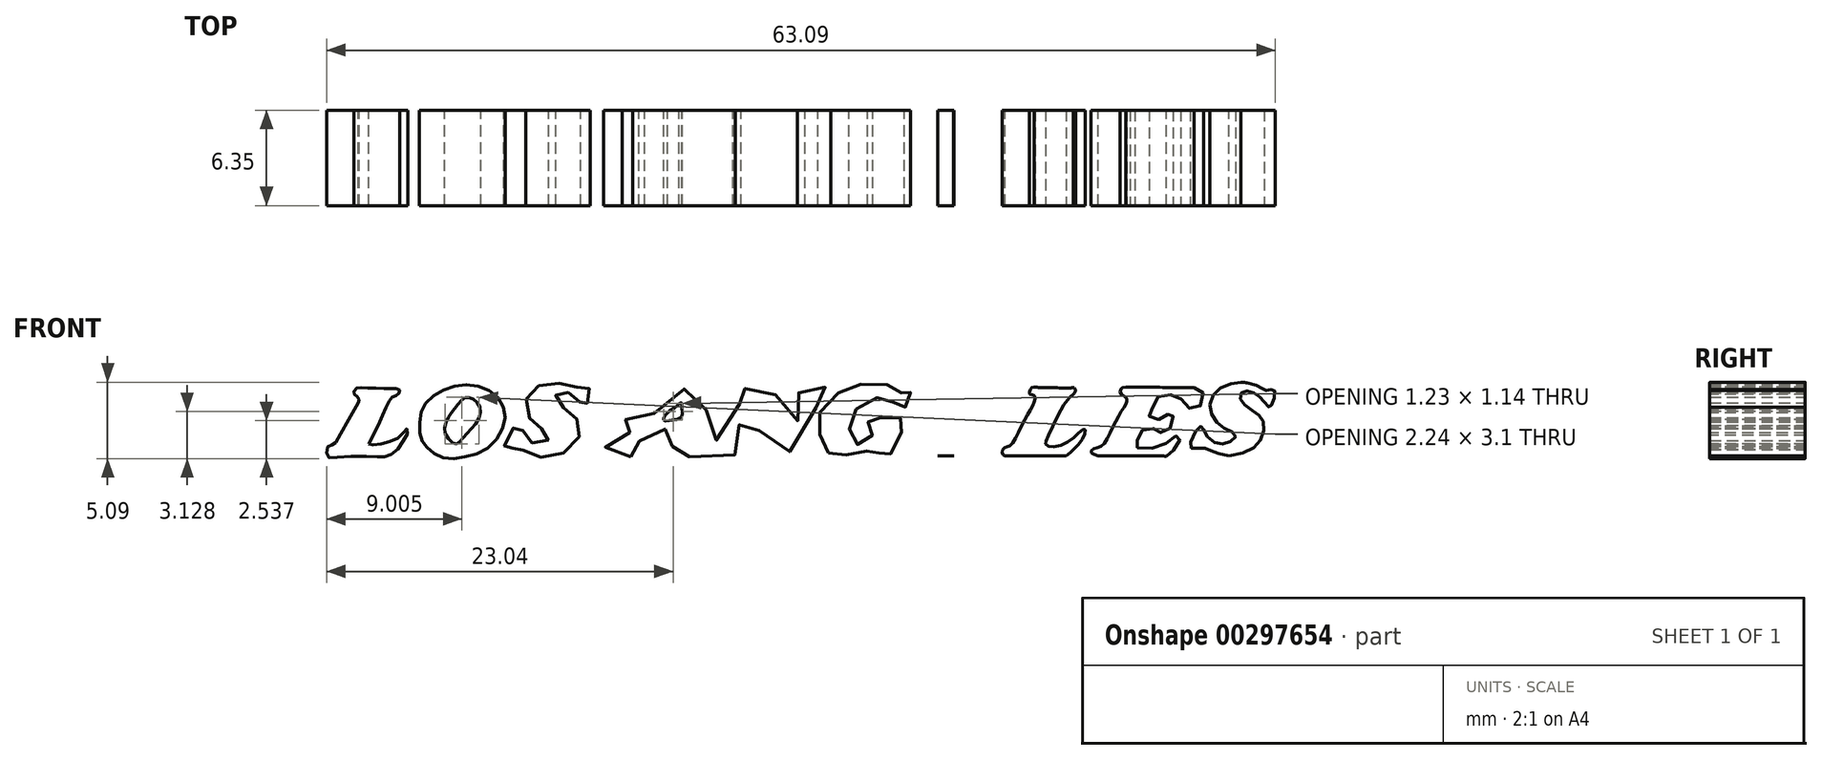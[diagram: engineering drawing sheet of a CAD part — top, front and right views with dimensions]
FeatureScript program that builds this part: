
annotation { "Feature Type Name" : "Feature", "Feature Type Description" : "" }
export const myFeature = defineFeature(function(context is Context, id is Id, definition is map)
    precondition{}
    {
        {
            var Q0;
            Q0=qCreatedBy(makeId("Front.planeOp"),FACE);
            var sketch = newSketch(context, id + "F0", { "sketchPlane" : qUnion([Q0])});
            skFitSpline(sketch, "E0", {"points": [v(-42.48, -14.81) * mm, v(-28.24, -14.72) * mm, v(-25.29, -14.85) * mm, v(-23.97, -14.75) * mm, v(-23, -13.63) * mm, v(-21.37, -10.74) * mm, v(-20.73, -9.87) * mm, v(-20.5, -9.65) * mm, v(-19.83, -9.62) * mm, v(-15.31, -9.65) * mm, v(-11.17, -9.59) * mm, v(-7.2, -9.59) * mm, v(-6.43, -9.55) * mm, v(-6.07, -9.4) * mm, v(-5.94, -9) * mm, v(-6.65, -8.5) * mm, v(-7.13, -8.34) * mm, v(-7.32, -7.4) * mm, v(-7.07, -6.73) * mm, v(-6.33, -5.29) * mm, v(-5.34, -3.5) * mm, v(-4.63, -2.34) * mm, v(-4.44, -1.86) * mm, v(-4.18, -1.82) * mm, v(-4.05, -2.63) * mm, v(-3.54, -5.03) * mm, v(-3.12, -7.28) * mm, v(-2.77, -8.75) * mm, v(-2.16, -9.36) * mm, v(-1.2, -9.65) * mm, v(0, -9.59) * mm, v(1.88, -9.62) * mm, v(5.82, -9.54) * mm, v(10.32, -9.56) * mm, v(13.02, -9.67) * mm, v(13.61, -9.46) * mm, v(13.97, -9.08) * mm, v(14.32, -8.5) * mm, v(15.19, -6.58) * mm, v(16.34, -4.98) * mm, v(16.5, -4.47) * mm, v(16.53, -4.15) * mm, v(16.25, -3.99) * mm, v(15.83, -4.08) * mm, v(15.44, -4.5) * mm, v(14.83, -5.46) * mm, v(13.78, -6.52) * mm, v(12.65, -7.48) * mm, v(10.66, -8.41) * mm, v(9.03, -8.73) * mm, v(7.97, -8.67) * mm, v(7.44, -8.56) * mm, v(7.4, -8.38) * mm], "startDerivative": vector(273.52, 3.73) * mm, "endDerivative": vector(-12.7, 24.43) * mm});
            skFitSpline(sketch, "E1", {"points": [v(7.44, -8.44) * mm, v(7.44, -8.2) * mm, v(7.92, -7) * mm, v(9.27, -4.42) * mm, v(10.18, -2.42) * mm, v(10.55, -1.82) * mm, v(10.84, -1.6) * mm, v(11.42, -1.56) * mm, v(12.06, -1.6) * mm, v(12.67, -1.9) * mm, v(12.96, -2.25) * mm, v(12.92, -2.7) * mm, v(12.88, -3.49) * mm, v(12.76, -4.05) * mm, v(12.68, -4.36) * mm, v(12.78, -4.47) * mm, v(12.99, -4.42) * mm, v(13.34, -3.97) * mm, v(13.95, -2.96) * mm, v(14.76, -1.27) * mm, v(15.53, 0) * mm, v(15.99, 0.7) * mm, v(16.13, 1) * mm, v(16.15, 1.25) * mm, v(16.01, 1.4) * mm, v(15.9, 1.45) * mm, v(15.66, 1.26) * mm, v(15.28, 0.84) * mm, v(14.37, 0) * mm, v(13.46, -0.47) * mm, v(12.76, -0.65) * mm, v(12, -0.67) * mm, v(11.63, -0.68) * mm, v(11.4, -0.65) * mm, v(11.36, -0.52) * mm, v(12.36, 1.44) * mm, v(13.45, 3.62) * mm, v(14.31, 5.29) * mm, v(14.58, 5.7) * mm, v(14.76, 5.9) * mm, v(15.05, 5.91) * mm, v(15.9, 5.98) * mm, v(16.5, 5.9) * mm, v(17.2, 5.64) * mm, v(17.6, 5.16) * mm, v(17.92, 4.58) * mm, v(18.2, 3.97) * mm, v(18.26, 3.22) * mm, v(18.2, 2.08) * mm, v(18.26, 1.4) * mm, v(18.2, 0.96) * mm, v(18.32, 0.6) * mm, v(18.51, 0.64) * mm, v(18.79, 0.57) * mm, v(18.93, 0.8) * mm, v(19.38, 1.55) * mm, v(20.07, 2.77) * mm, v(20.66, 4.09) * mm, v(21.34, 5.22) * mm, v(21.5, 5.76) * mm, v(21.54, 6.1) * mm, v(21.34, 6.27) * mm, v(21.08, 6.47) * mm, v(20.77, 6.57) * mm, v(19.49, 6.7) * mm, v(16.14, 6.73) * mm, v(12.2, 6.72) * mm, v(9.7, 6.72) * mm, v(6.33, 6.73) * mm, v(3.18, 6.68) * mm, v(2.75, 6.57) * mm, v(2.51, 6.4) * mm, v(2.52, 6.12) * mm, v(2.71, 5.9) * mm, v(3.13, 5.87) * mm, v(3.44, 5.8) * mm, v(3.66, 5.53) * mm, v(3.67, 5.15) * mm, v(3.64, 4.77) * mm, v(3.3, 4.29) * mm, v(2.08, 3.33) * mm, v(0.18, 1.83) * mm, v(-1.6, 0.31) * mm, v(-3.38, -1.03) * mm, v(-3.86, -1.4) * mm, v(-4.07, -1.46) * mm, v(-4.09, -1.28) * mm, v(-3.65, -0.38) * mm, v(-2.39, 1.92) * mm, v(-1, 4.38) * mm, v(-0.37, 5.4) * mm, v(0, 5.68) * mm, v(0.18, 5.76) * mm, v(0.52, 5.85) * mm, v(0.7, 6.18) * mm, v(0.55, 6.48) * mm, v(0.3, 6.6) * mm, v(-1.63, 6.66) * mm, v(-4.09, 6.67) * mm, v(-5.35, 6.69) * mm, v(-5.8, 6.6) * mm, v(-6.06, 6.32) * mm, v(-6.01, 6.05) * mm, v(-5.58, 5.85) * mm, v(-5.27, 5.87) * mm, v(-5.05, 5.65) * mm, v(-4.95, 5.33) * mm, v(-5.32, 4.5) * mm, v(-5.85, 3.5) * mm, v(-6.22, 2.82) * mm, v(-6.62, 2.45) * mm, v(-7.05, 2.23) * mm, v(-7.97, 2.25) * mm, v(-8.79, 2.23) * mm, v(-8.9, 2.07) * mm, v(-8.85, 1.83) * mm, v(-8.6, 1.84) * mm, v(-8.02, 1.83) * mm, v(-7.55, 1.84) * mm, v(-7.2, 1.83) * mm, v(-7.09, 1.65) * mm, v(-7.17, 1.28) * mm, v(-7.55, 0.66) * mm, v(-8.9, -1.88) * mm, v(-10.07, -4) * mm, v(-11.27, -6.17) * mm, v(-11.82, -7.2) * mm, v(-12.19, -7.86) * mm, v(-12.5, -8) * mm, v(-12.8, -7.9) * mm, v(-13.06, -7.6) * mm, v(-13, -6.91) * mm, v(-12.78, -4.46) * mm, v(-12.28, -0.5) * mm, v(-12.08, 0.88) * mm, v(-11.7, 3.87) * mm, v(-11.37, 5.8) * mm, v(-11.34, 6.47) * mm, v(-11.82, 6.63) * mm, v(-12.66, 6.66) * mm, v(-14, 6.72) * mm, v(-14.87, 6.69) * mm, v(-15.35, 6.11) * mm, v(-15.7, 5.53) * mm, v(-16.06, 5.21) * mm, v(-16.31, 5.02) * mm, v(-17.02, 4.96) * mm, v(-18.2, 4.99) * mm, v(-18.75, 5.02) * mm, v(-19.07, 4.93) * mm, v(-19.07, 4.67) * mm, v(-18.75, 4.57) * mm, v(-17.85, 4.48) * mm, v(-17.24, 4.6) * mm, v(-16.86, 4.54) * mm, v(-16.73, 4.35) * mm, v(-17.15, 3.9) * mm, v(-17.76, 3.03) * mm, v(-18.59, 2) * mm, v(-19.17, 1.3) * mm, v(-19.42, 0.98) * mm, v(-19.96, 1.14) * mm, v(-20.61, 1.2) * mm, v(-20.61, 0.71) * mm, v(-20.13, 0.55) * mm, v(-20.02, 0) * mm, v(-20.93, -0.75) * mm, v(-21.31, -1.4) * mm, v(-21.9, -2.04) * mm, v(-22.44, -2.47) * mm, v(-23.1, -2.63) * mm, v(-24.06, -2.63) * mm, v(-24.82, -2.63) * mm, v(-24.98, -3.12) * mm, v(-24.44, -3.17) * mm, v(-23.47, -3.17) * mm, v(-22.98, -3.17) * mm, v(-22.98, -3.66) * mm, v(-23.85, -4.52) * mm, v(-25.41, -6.73) * mm, v(-26.98, -7.97) * mm, v(-28.86, -8.38) * mm, v(-29.89, -8.38) * mm, v(-30.16, -8.38) * mm], "startDerivative": vector(-10.83, 69.52) * mm, "endDerivative": vector(-71.75, -1.4) * mm});
            skFitSpline(sketch, "E2", {"points": [v(-30.08, -8.38) * mm, v(-30.08, -8.3) * mm, v(-30, -7.95) * mm, v(-29.4, -6.79) * mm, v(-27.7, -3.74) * mm, v(-26.8, -1.97) * mm], "startDerivative": vector(-0.07, 1.23) * mm, "endDerivative": vector(2.98, 6) * mm});
            skFitSpline(sketch, "E3", {"points": [v(-27.06, -2.5) * mm, v(-25.93, -0.4) * mm, v(-21.3, 7.98) * mm, v(-19.13, 11.83) * mm, v(-18.61, 13.05) * mm, v(-18.16, 13.44) * mm, v(-17.72, 13.56) * mm, v(-17.2, 13.56) * mm, v(-15.53, 13.56) * mm, v(-14.7, 13.56) * mm, v(-14.44, 13.95) * mm, v(-14.76, 14.46) * mm, v(-15.08, 14.4) * mm], "startDerivative": vector(8.16, 15.32) * mm, "endDerivative": vector(-7.86, -4.11) * mm});
            skFitSpline(sketch, "E4", {"points": [v(-14.98, 14.45) * mm, v(-17.8, 14.45) * mm, v(-21.12, 14.45) * mm, v(-22.1, 14.45) * mm, v(-22.48, 14.45) * mm], "startDerivative": vector(-8.05, 0) * mm, "endDerivative": vector(-2.9, 0) * mm});
            skFitSpline(sketch, "E5", {"points": [v(-22.37, 14.45) * mm, v(-23.1, 14.45) * mm, v(-25.49, 14.4) * mm, v(-27.37, 14.45) * mm, v(-27.96, 14.45) * mm, v(-28.32, 14.4) * mm, v(-28.5, 13.92) * mm, v(-28.03, 13.5) * mm, v(-27.06, 13.49) * mm, v(-25.94, 13.54) * mm, v(-25.24, 13.58) * mm, v(-24.8, 13.4) * mm, v(-24.54, 13.02) * mm, v(-24.72, 12.63) * mm, v(-24.85, 12.31) * mm, v(-25.26, 12) * mm, v(-25.85, 11.95) * mm, v(-27.06, 11.97) * mm, v(-28.84, 12) * mm, v(-29.75, 12.06) * mm, v(-30.08, 11.84) * mm, v(-29.8, 11.65) * mm, v(-29.25, 11.6) * mm, v(-27.9, 11.56) * mm, v(-26.2, 11.59) * mm, v(-25.47, 11.56) * mm, v(-25.58, 11.31) * mm, v(-25.71, 10.8) * mm, v(-25.99, 10.27) * mm, v(-26.12, 10.13) * mm, v(-26.64, 10.09) * mm, v(-27.3, 9.95) * mm, v(-27.91, 9.95) * mm, v(-28.3, 9.98) * mm, v(-28.73, 9.84) * mm, v(-28.64, 9.73) * mm], "startDerivative": vector(-20.9, 0.36) * mm, "endDerivative": vector(11.96, -8.74) * mm});
            skFitSpline(sketch, "E6", {"points": [v(-28.7, 9.77) * mm, v(-28.25, 9.68) * mm, v(-27.2, 9.69) * mm, v(-26.54, 9.6) * mm, v(-26.54, 9.3) * mm, v(-26.95, 8.54) * mm, v(-27.51, 7.6) * mm, v(-27.88, 6.97) * mm, v(-28.03, 6.7) * mm, v(-28.25, 6.68) * mm, v(-28.95, 6.7) * mm, v(-29.34, 6.65) * mm, v(-29.52, 6.45) * mm, v(-29.4, 6.27) * mm, v(-29, 6.23) * mm, v(-28.7, 6.2) * mm, v(-28.45, 6.2) * mm, v(-28.38, 5.95) * mm, v(-28.87, 4.9) * mm, v(-29.52, 3.75) * mm, v(-30.08, 3.4) * mm, v(-31.8, 3.45) * mm, v(-34.51, 3.45) * mm, v(-34.97, 3.45) * mm, v(-34.7, 3.07) * mm, v(-33.37, 3.03) * mm, v(-31.54, 3.03) * mm, v(-30.7, 3) * mm, v(-30.08, 2.56) * mm, v(-30.85, 1.58) * mm, v(-31.5, 0) * mm, v(-32.15, -0.98) * mm, v(-32.38, -1.4) * mm, v(-33.79, -1.47) * mm, v(-35.89, -1.4) * mm, v(-37.3, -1.55) * mm, v(-37.53, -1.74) * mm, v(-37.07, -1.93) * mm, v(-35.93, -1.93) * mm, v(-34.02, -1.93) * mm, v(-32.68, -2.04) * mm, v(-33.22, -3.04) * mm, v(-33.87, -4.33) * mm, v(-34.4, -4.71) * mm, v(-36.04, -4.8) * mm, v(-36.57, -5.02) * mm, v(-36.15, -5.21) * mm, v(-35.28, -5.13) * mm, v(-34.51, -5.25) * mm, v(-34.74, -6.2) * mm, v(-35.31, -7.3) * mm, v(-35.81, -8.38) * mm, v(-36.27, -8.38) * mm, v(-36.46, -8.76) * mm, v(-37.1, -8.38) * mm, v(-37.45, -8.38) * mm, v(-37.72, -8.54) * mm, v(-38.7, -8.64) * mm, v(-41.78, -8.56) * mm, v(-43.18, -8.59) * mm, v(-43.63, -8.62) * mm, v(-43.74, -8.96) * mm, v(-43.39, -9.1) * mm, v(-41.1, -9.02) * mm, v(-38.53, -9) * mm, v(-37.13, -9.08) * mm, v(-36.67, -9.13) * mm, v(-36.65, -9.58) * mm, v(-36.9, -10.06) * mm, v(-37.3, -10.8) * mm, v(-37.48, -11.27) * mm, v(-37.77, -11.43) * mm, v(-38.33, -11.44) * mm, v(-39.1, -11.44) * mm, v(-39.52, -11.47) * mm, v(-39.87, -11.5) * mm, v(-39.84, -11.73) * mm, v(-39.4, -11.81) * mm, v(-38.8, -11.8) * mm, v(-38.33, -11.81) * mm, v(-37.96, -11.99) * mm, v(-38.19, -12.6) * mm, v(-38.48, -13.1) * mm, v(-38.85, -13.66) * mm, v(-39.34, -13.86) * mm, v(-40.92, -13.9) * mm, v(-42.38, -13.86) * mm, v(-43.39, -13.94) * mm, v(-43.55, -14.38) * mm, v(-43.07, -14.8) * mm, v(-42.48, -14.81) * mm, v(-36.86, -14.74) * mm], "startDerivative": vector(47.36, -12.11) * mm, "endDerivative": vector(245.75, 0.9) * mm});
            skFitSpline(sketch, "E7", {"points": [v(-30.75, -9.52) * mm, v(-31.52, -11.02) * mm, v(-32.3, -12.42) * mm, v(-32.75, -13.2) * mm, v(-32.57, -13.6) * mm, v(-30.72, -13.6) * mm, v(-28.7, -13.55) * mm, v(-24.84, -12.25) * mm, v(-22.37, -9.5) * mm, v(-20.68, -7.61) * mm, v(-20.04, -7.18) * mm, v(-19.5, -7.34) * mm, v(-19.84, -8.07) * mm, v(-20.1, -8.8) * mm, v(-19.65, -8.9) * mm, v(-18.85, -8.38) * mm, v(-17.63, -7.61) * mm, v(-17.2, -6) * mm, v(-17.06, -4.44) * mm, v(-16.83, -3.45) * mm, v(-17.02, -3.26) * mm], "startDerivative": vector(-13.55, -26.1) * mm, "endDerivative": vector(-11, 6.01) * mm});
            skFitSpline(sketch, "E8", {"points": [v(-16.93, -3.3) * mm, v(-19.15, -3.2) * mm, v(-20.82, -3.18) * mm, v(-21.16, -3.17) * mm, v(-21.5, -3.3) * mm, v(-22.04, -3.9) * mm, v(-23.44, -5.73) * mm, v(-24.3, -6.92) * mm, v(-24.38, -7.58) * mm, v(-23.95, -8.38) * mm, v(-23.14, -8.66) * mm, v(-22.89, -8.8) * mm, v(-22.74, -9.2) * mm, v(-23.02, -9.52) * mm, v(-24.93, -9.57) * mm, v(-27.37, -9.54) * mm, v(-29.33, -9.54) * mm, v(-30.53, -9.52) * mm, v(-30.87, -9.74) * mm, v(-31, -10.01) * mm], "startDerivative": vector(-27.61, 1.9) * mm, "endDerivative": vector(-4, -9.47) * mm});
            skFitSpline(sketch, "E9", {"points": [v(-16.23, -1.88) * mm, v(-15.71, 1.78) * mm, v(-15.47, 4.3) * mm, v(-15.54, 4.5) * mm, v(-15.75, 4.35) * mm, v(-17.1, 2.55) * mm, v(-19.5, -0.5) * mm, v(-20.51, -1.88) * mm, v(-20.84, -2.26) * mm, v(-20.8, -2.5) * mm, v(-20.5, -2.5) * mm, v(-17.95, -2.5) * mm, v(-16.73, -2.5) * mm, v(-16.44, -2.26) * mm, v(-16.23, -1.88) * mm]});
            skFitSpline(sketch, "E10", {"points": [v(1.07, -5.96) * mm, v(1.27, -7.53) * mm, v(1.52, -8.38) * mm, v(2.16, -8.38) * mm, v(2.61, -8.38) * mm, v(3.58, -6.73) * mm, v(5.28, -3.45) * mm, v(6, -2.1) * mm, v(6.2, -1.88) * mm, v(6.09, -1.6) * mm, v(5.52, -1.64) * mm, v(4.63, -1.64) * mm, v(4.1, -1.53) * mm, v(3.93, -1.23) * mm, v(4.23, -1.1) * mm, v(4.88, -1.07) * mm, v(5.74, -1.04) * mm, v(6.28, -1.02) * mm, v(6.71, -0.7) * mm, v(7.57, 1.09) * mm, v(8.65, 3.03) * mm, v(9.06, 3.95) * mm, v(9.2, 4.27) * mm, v(9.16, 4.35) * mm], "startDerivative": vector(3.52, -26.38) * mm, "endDerivative": vector(-3.04, 5.01) * mm});
            skFitSpline(sketch, "E11", {"points": [v(9.18, 4.33) * mm, v(8.96, 4.38) * mm, v(8.41, 4.37) * mm, v(8.1, 4.4) * mm, v(7.93, 4.58) * mm, v(8.02, 4.78) * mm, v(8.52, 4.85) * mm, v(9.45, 4.91) * mm, v(9.72, 5.13) * mm, v(9.92, 5.63) * mm, v(9.7, 6) * mm, v(8.95, 6.23) * mm, v(7.84, 6.24) * mm, v(6.62, 5.65) * mm, v(2.67, 2.67) * mm, v(0.49, 0.94) * mm, v(0, 0.55) * mm, v(0, -0.2) * mm, v(0.2, -1.54) * mm, v(1.14, -6.49) * mm], "startDerivative": vector(-7.21, 2.57) * mm, "endDerivative": vector(9.26, -47.07) * mm});
            skFitSpline(sketch, "E12", {"points": [v(17.72, -7.86) * mm, v(19.58, -4.4) * mm, v(20.03, -3.45) * mm, v(19.77, -3.45) * mm, v(19.16, -3.45) * mm, v(18.65, -2.63) * mm, v(19.26, -2.63) * mm, v(20.15, -2.63) * mm, v(20.96, -1.88) * mm, v(22.11, 0) * mm, v(22.46, 1) * mm, v(22.17, 1.25) * mm, v(21.3, 1.31) * mm, v(20.86, 1.5) * mm, v(20.99, 1.9) * mm, v(22.01, 1.9) * mm, v(22.85, 2.02) * mm, v(23.65, 2.98) * mm, v(24.58, 4.81) * mm, v(24.55, 5.52) * mm, v(24.03, 5.8) * mm, v(23.3, 6) * mm, v(23.68, 6.67) * mm, v(24.68, 6.7) * mm, v(28.14, 6.7) * mm, v(30.23, 6.7) * mm], "startDerivative": vector(25.72, 49.44) * mm, "endDerivative": vector(32.68, -0.46) * mm});
            skFitSpline(sketch, "E13", {"points": [v(29.61, 6.71) * mm, v(30.58, 6.71) * mm, v(32.31, 6.7) * mm, v(34.3, 6.07) * mm, v(35.53, 4.92) * mm, v(36.05, 3.32) * mm, v(35.55, 1.71) * mm, v(34.03, -0.12) * mm, v(32.44, -1.2) * mm, v(31.43, -1.6) * mm], "startDerivative": vector(10.63, -0.2) * mm, "endDerivative": vector(-10.71, -3.89) * mm});
            skFitSpline(sketch, "E14", {"points": [v(31.75, -1.5) * mm, v(30.07, -1.95) * mm, v(29.8, -2.03) * mm, v(29.76, -2.23) * mm, v(30.39, -3.03) * mm, v(31.06, -3.99) * mm, v(31.32, -4.44) * mm], "startDerivative": vector(-7.74, -2.3) * mm, "endDerivative": vector(1.6, -2.9) * mm});
            skFitSpline(sketch, "E15", {"points": [v(31.32, -4.44) * mm, v(32.45, -6.49) * mm, v(33.08, -7.7) * mm, v(33.3, -8.38) * mm, v(33.58, -7.88) * mm, v(33.85, -7.43) * mm, v(33.72, -7.11) * mm, v(33.67, -6.73) * mm, v(34.17, -6.73) * mm, v(34.76, -5.96) * mm, v(35.26, -5.13) * mm, v(35.85, -4.03) * mm, v(36.21, -3.45) * mm, v(36.48, -3.8) * mm, v(36.17, -4.44) * mm, v(36.03, -5.96) * mm, v(36.21, -7.52) * mm, v(37.48, -8.38) * mm, v(38.7, -9.02) * mm, v(40.8, -8.38) * mm, v(41.52, -7.3) * mm, v(41.61, -6.73) * mm, v(41.11, -6.73) * mm, v(40.88, -6.73) * mm], "startDerivative": vector(16.87, -31.7) * mm, "endDerivative": vector(-8.38, 0.83) * mm});
            skFitSpline(sketch, "E16", {"points": [v(40.95, -6.74) * mm, v(40.88, -6.49) * mm, v(41.42, -6.34) * mm, v(41.83, -6.1) * mm, v(41.68, -5.46) * mm, v(40.5, -3.45) * mm, v(40.02, -2.92) * mm, v(39.7, -2.83) * mm, v(38.54, -2.78) * mm, v(36.74, -2.8) * mm, v(35.92, -2.81) * mm, v(35.68, -2.63) * mm, v(35.82, -2.4) * mm, v(37.05, -2.31) * mm, v(38.75, -2.33) * mm, v(39.27, -2.33) * mm, v(39.42, -2.13) * mm, v(38.83, -1.5) * mm, v(38.36, -0.85) * mm, v(38.09, -0.5) * mm, v(37.65, -0.5) * mm, v(36.89, -0.5) * mm, v(36.96, -0.16) * mm, v(37.38, 0) * mm, v(37.86, 0) * mm, v(37.73, 0.4) * mm, v(37.52, 1.14) * mm, v(37.54, 2.64) * mm, v(37.86, 3.64) * mm, v(37.7, 3.88) * mm, v(37.3, 3.88) * mm, v(37.12, 4.27) * mm, v(37.36, 4.27) * mm, v(37.96, 4.27) * mm, v(38.16, 4.33) * mm, v(38.5, 4.7) * mm, v(39.48, 5.89) * mm, v(41.52, 6.7) * mm, v(43.01, 6.95) * mm, v(44.98, 6.71) * mm, v(46.55, 5.95) * mm, v(46.95, 5.63) * mm, v(47.63, 5.6) * mm, v(48.92, 5.82) * mm, v(49.49, 5.95) * mm, v(49.68, 5.66) * mm, v(49.2, 4.58) * mm, v(47.87, 2.15) * mm, v(46.95, 0.5) * mm, v(46.57, 0.56) * mm, v(46.38, 1) * mm, v(46.52, 1.67) * mm, v(46.63, 2.4) * mm, v(46.47, 2.72) * mm, v(45.93, 2.72) * mm, v(45.74, 2.9) * mm, v(45.87, 3.15) * mm, v(46.28, 3.18) * mm, v(46.68, 3.37) * mm, v(46.3, 4.69) * mm, v(44.6, 5.77) * mm, v(42.58, 5.85) * mm, v(41.53, 4.33) * mm, v(41.77, 1.96) * mm, v(43.26, 0) * mm, v(45.1, -2.24) * mm, v(45.71, -3.92) * mm, v(45.74, -6.49) * mm, v(43.31, -9.21) * mm, v(40.18, -10.01) * mm, v(36.83, -9.26) * mm, v(35.99, -8.73) * mm, v(34.97, -8.69) * mm, v(34.17, -8.82) * mm, v(33.79, -9.14) * mm, v(34.1, -10.62) * mm, v(34.62, -12.32) * mm, v(36.4, -14.45) * mm, v(40.02, -15.86) * mm, v(44.04, -14.81) * mm, v(45.87, -13.84) * mm, v(46.17, -13.52) * mm, v(45.85, -13.4) * mm, v(45.26, -13.36) * mm, v(45.2, -13.04) * mm, v(45.58, -12.95) * mm, v(46.4, -12.9) * mm, v(47, -12.98) * mm, v(47.64, -12.39) * mm, v(49.35, -10.64) * mm, v(50.2, -9.66) * mm, v(50.2, -9.46) * mm, v(49.6, -9.44) * mm, v(49.37, -9.21) * mm, v(49.66, -9.03) * mm, v(50.46, -8.96) * mm, v(51.55, -7.87) * mm, v(52.57, -5.96) * mm, v(52.5, -5.96) * mm, v(51.64, -5.58) * mm, v(51.82, -5.13) * mm, v(52.86, -5.13) * mm, v(53.16, -4.79) * mm, v(53.43, -4.44) * mm, v(53.59, -5.03) * mm, v(53.47, -5.74) * mm, v(49.98, -10.93) * mm, v(46.2, -14.54) * mm, v(43.31, -16.3) * mm, v(41.36, -16.97) * mm, v(38.8, -17.38) * mm, v(36.24, -17.28) * mm, v(33.67, -16.47) * mm, v(30.61, -14.34) * mm, v(29.34, -12.45) * mm], "startDerivative": vector(-35.74, 67.07) * mm, "endDerivative": vector(-78.38, 147.46) * mm});
            skFitSpline(sketch, "E17", {"points": [v(29.67, -13.08) * mm, v(28.81, -11.23) * mm, v(28.52, -10.91) * mm, v(26.2, -10.91) * mm, v(25.24, -10.72) * mm, v(25.76, -10.01) * mm, v(26.5, -10.42) * mm, v(27.87, -10.4) * mm, v(28.43, -10.3) * mm, v(28.36, -8.61) * mm, v(28.26, -7.42) * mm, v(28.04, -7.08) * mm, v(26.81, -7.01) * mm, v(25.63, -7.03) * mm, v(25.25, -6.94) * mm, v(25.09, -6.74) * mm, v(25.28, -6.49) * mm, v(26.18, -6.49) * mm, v(27.37, -6.49) * mm, v(27.9, -6.49) * mm, v(28.07, -5.96) * mm, v(27.92, -5.03) * mm, v(27.52, -3.12) * mm, v(26.9, -1.88) * mm, v(26.43, -1.5) * mm, v(25.78, -1.5) * mm, v(25.04, -2.85) * mm, v(23.76, -5.28) * mm, v(22.85, -6.92) * mm, v(22.4, -7.77) * mm, v(22.43, -8.25) * mm, v(22.79, -8.38) * mm, v(23.3, -8.8) * mm, v(23.3, -9.36) * mm, v(22.71, -9.6) * mm, v(19.55, -9.6) * mm, v(16.24, -9.6) * mm, v(15.46, -9.3) * mm, v(15.6, -8.81) * mm, v(15.94, -8.67) * mm, v(16.92, -8.58) * mm, v(17.5, -8.06) * mm, v(17.72, -7.86) * mm], "startDerivative": vector(-29.8, 63.93) * mm, "endDerivative": vector(14.63, 12.6) * mm});
            skFitSpline(sketch, "E18", {"points": [v(26.55, 0.3) * mm, v(27.9, -0.7) * mm, v(29.1, 0) * mm, v(30.43, 1.73) * mm, v(31.1, 3.35) * mm], "startDerivative": vector(5.54, -5.84) * mm, "endDerivative": vector(2.2, 6.42) * mm});
            skFitSpline(sketch, "E19", {"points": [v(30.92, 2.8) * mm, v(31.32, 4.13) * mm, v(31.2, 5.26) * mm, v(30.59, 5.87) * mm], "startDerivative": vector(1.33, 3.53) * mm, "endDerivative": vector(-2.42, 1.77) * mm});
            skFitSpline(sketch, "E20", {"points": [v(27, -0.18) * mm, v(26.55, 0.3) * mm, v(26.9, 0.83) * mm, v(27.9, 2.8) * mm, v(29.13, 5.02) * mm, v(29.61, 5.87) * mm, v(30.1, 6.02) * mm, v(30.59, 5.87) * mm], "startDerivative": vector(-5.8, 4.27) * mm, "endDerivative": vector(4.84, -2.02) * mm});
            skLineSegment(sketch, "E21", {"start": v(7.44, -8.44) * mm, "end": v(7.44, -8.44) * mm});
            skFitSpline(sketch, "E22", {"points": [v(26.55, 0.3) * mm, v(26.64, 0.5) * mm, v(26.9, 0.83) * mm], "startDerivative": vector(0.15, 0.47) * mm, "endDerivative": vector(0.54, 0.58) * mm});
            skFitSpline(sketch, "E23", {"points": [v(-14.98, 14.45) * mm, v(-14.96, 14.46) * mm], "startDerivative": vector(0.02, 0) * mm, "endDerivative": vector(0.02, 0) * mm});
            skFitSpline(sketch, "E24", {"points": [v(-27.06, -2.5) * mm, v(-27.08, -2.55) * mm], "startDerivative": vector(-0.04, -0.04) * mm, "endDerivative": vector(-0.04, -0.04) * mm});
            skFitSpline(sketch, "E25", {"points": [v(-27.07, -2.5) * mm, v(-27.06, -2.5) * mm], "startDerivative": vector(0.01, 0) * mm, "endDerivative": vector(0.01, 0) * mm});
            skFitSpline(sketch, "E26", {"points": [v(-30.08, -8.38) * mm, v(-30.08, -8.38) * mm], "startDerivative": vector(0, 0) * mm, "endDerivative": vector(0, 0) * mm});
            skFitSpline(sketch, "E27", {"points": [v(7.44, -8.44) * mm, v(7.42, -8.47) * mm], "startDerivative": vector(0, -0.02) * mm, "endDerivative": vector(0, -0.02) * mm});
            skFitSpline(sketch, "E28", {"points": [v(7.42, 6.72) * mm, v(7.42, -8.47) * mm], "startDerivative": vector(0, 0) * mm, "endDerivative": vector(0, 0) * mm});
            skFitSpline(sketch, "E29", {"points": [v(7.43, -8.5) * mm, v(7.43, -8.35) * mm], "startDerivative": vector(-0.04, 0.15) * mm, "endDerivative": vector(-0.04, 0.15) * mm});
            skFitSpline(sketch, "E30", {"points": [v(28.78, 10.97) * mm, v(28.94, 10.75) * mm, v(29.02, 10.51) * mm], "startDerivative": vector(0.36, -0.4) * mm, "endDerivative": vector(0.12, -0.5) * mm});
            skFitSpline(sketch, "E31", {"points": [v(30.59, 5.87) * mm, v(30.59, 5.13) * mm, v(30.83, 4.05) * mm, v(31.09, 3.24) * mm], "startDerivative": vector(-0.15, -2.3) * mm, "endDerivative": vector(0.78, -2.34) * mm});
            skFitSpline(sketch, "E32", {"points": [v(31.43, -1.6) * mm, v(31.43, -2.42) * mm, v(31.1, -3.4) * mm, v(31.24, -3.68) * mm, v(31.24, -4.3) * mm, v(31.26, -4.33) * mm], "startDerivative": vector(0.46, -2.87) * mm, "endDerivative": vector(0.34, -0.28) * mm});
            skFitSpline(sketch, "E33", {"points": [v(29.34, -12.45) * mm, v(28.91, -13.47) * mm, v(27.2, -16.92) * mm, v(24.46, -20.87) * mm, v(16.08, -27.81) * mm, v(11.32, -29.63) * mm, v(3.84, -31.14) * mm, v(-2.35, -30.83) * mm, v(-9, -29.55) * mm, v(-15.94, -25.47) * mm, v(-20.55, -21.02) * mm, v(-23.34, -16.49) * mm, v(-23.97, -14.75) * mm], "startDerivative": vector(-8.88, -22.38) * mm, "endDerivative": vector(-9.26, 31.23) * mm});
            skFitSpline(sketch, "E34", {"points": [v(-24.84, -12.25) * mm, v(-25.46, -10.67) * mm, v(-25.82, -9.54) * mm], "startDerivative": vector(-1.24, 3) * mm, "endDerivative": vector(-0.71, 2.36) * mm});
            skFitSpline(sketch, "E35", {"points": [v(-26.76, -1.95) * mm, v(-26.87, -3.12) * mm, v(-26.66, -5.17) * mm, v(-26.5, -6.42) * mm, v(-26.27, -7.58) * mm], "startDerivative": vector(-0.75, -4.62) * mm, "endDerivative": vector(1.06, -5.1) * mm});
            skFitSpline(sketch, "E36", {"points": [v(7.12, -11.43) * mm, v(9.27, -17.58) * mm, v(10.58, -22.34) * mm, v(12.06, -27.5) * mm, v(12.96, -29.18) * mm], "startDerivative": vector(7.76, -21.32) * mm, "endDerivative": vector(5.48, -8.5) * mm});
            skFitSpline(sketch, "E37", {"points": [v(-13.62, -11.3) * mm, v(-12.77, -14.3) * mm, v(-11.06, -17.76) * mm, v(-8.55, -22.88) * mm, v(-5.59, -27.28) * mm, v(-2.35, -30.83) * mm], "startDerivative": vector(4.16, -18.18) * mm, "endDerivative": vector(16.04, -16.66) * mm});
            skFitSpline(sketch, "E38", {"points": [v(-10.5, 13.44) * mm, v(-11.95, 10.87) * mm, v(-12.13, 10.66) * mm, v(-12.45, 10.58) * mm, v(-12.59, 10.26) * mm, v(-12.5, 9.83) * mm, v(-11.87, 9.83) * mm, v(-9.44, 9.86) * mm, v(-8.77, 9.86) * mm, v(-8.13, 10.1) * mm, v(-7.51, 10.87) * mm, v(-7.2, 11.54) * mm, v(-7.3, 11.73) * mm, v(-7.6, 11.3) * mm, v(-8.34, 10.87) * mm, v(-9.22, 10.66) * mm, v(-9.76, 10.66) * mm, v(-9.78, 10.74) * mm], "startDerivative": vector(-14.88, -26.48) * mm, "endDerivative": vector(0, 4.36) * mm});
            skFitSpline(sketch, "E39", {"points": [v(-9.78, 10.7) * mm, v(-9.28, 11.7) * mm, v(-9.07, 12.11) * mm, v(-8.54, 13.35) * mm, v(-8.18, 13.86) * mm, v(-7.85, 13.98) * mm, v(-7.73, 14.26) * mm, v(-7.97, 14.39) * mm, v(-8.83, 14.4) * mm, v(-10.18, 14.45) * mm, v(-10.65, 14.4) * mm, v(-10.78, 14.07) * mm, v(-10.6, 13.9) * mm, v(-10.43, 13.66) * mm, v(-10.5, 13.44) * mm], "startDerivative": vector(5.48, 11.15) * mm, "endDerivative": vector(-2.55, -4.7) * mm});
            skFitSpline(sketch, "E40", {"points": [v(-4.7, 11.4) * mm, v(-4.55, 12.39) * mm, v(-4.01, 13.15) * mm, v(-3.4, 13.75) * mm, v(-2.9, 13.72) * mm, v(-2.35, 13.02) * mm, v(-2.77, 11.94) * mm, v(-3.6, 11.02) * mm, v(-4.01, 10.7) * mm, v(-4.7, 11.4) * mm]});
            skFitSpline(sketch, "E41", {"points": [v(-5.91, 10.48) * mm, v(-6.32, 11.09) * mm, v(-6.39, 12.26) * mm, v(-6, 13.4) * mm, v(-4.86, 14.26) * mm, v(-3.28, 14.64) * mm, v(-1.69, 14.2) * mm, v(-0.8, 13.09) * mm, v(-0.9, 11.72) * mm, v(-2.04, 10.33) * mm, v(-3.69, 9.79) * mm, v(-5, 9.82) * mm, v(-5.91, 10.48) * mm]});
            skFitSpline(sketch, "E42", {"points": [v(0.47, 10.3) * mm, v(1.55, 9.85) * mm, v(3.1, 10.07) * mm, v(4.22, 11.25) * mm, v(4.12, 12.26) * mm, v(3.33, 13) * mm, v(2.88, 13.4) * mm, v(2.66, 14) * mm, v(3.23, 14.2) * mm, v(3.9, 13.85) * mm, v(4.34, 13.4) * mm, v(4.63, 13.21) * mm, v(4.82, 13.7) * mm, v(4.88, 14.39) * mm, v(4.38, 14.36) * mm, v(3.93, 14.55) * mm, v(2.82, 14.74) * mm, v(1.49, 14.55) * mm, v(0.72, 13.82) * mm, v(0.82, 12.58) * mm, v(1.33, 11.98) * mm, v(2, 11.5) * mm, v(2.15, 11) * mm, v(1.4, 10.7) * mm, v(0.66, 11.12) * mm, v(0.37, 11.75) * mm, v(0, 11.91) * mm, v(-0.55, 11.06) * mm, v(-0.77, 10.36) * mm, v(-0.3, 10.39) * mm, v(0, 10.55) * mm, v(0.47, 10.3) * mm]});
            skFitSpline(sketch, "E43", {"points": [v(7.65, 9.85) * mm, v(6.22, 9.88) * mm, v(5.84, 10.13) * mm, v(6.03, 10.55) * mm, v(6.5, 10.61) * mm, v(7.2, 11.15) * mm, v(7.61, 11.53) * mm, v(7.74, 11.72) * mm, v(7.17, 11.79) * mm, v(7.1, 12.23) * mm, v(7.49, 12.33) * mm, v(8.47, 12.36) * mm, v(8.7, 12.39) * mm, v(9.33, 12.87) * mm, v(10.22, 13.63) * mm, v(11.14, 14.33) * mm, v(11.46, 14.55) * mm, v(12.19, 14.23) * mm, v(12.76, 12.45) * mm, v(13.01, 11.6) * mm, v(13.17, 11.06) * mm, v(13.46, 10.96) * mm, v(14.12, 12.2) * mm, v(14.98, 13.6) * mm, v(14.85, 13.91) * mm, v(14.6, 14.3) * mm, v(15.01, 14.39) * mm, v(16.06, 14.45) * mm, v(16.82, 14.39) * mm, v(17.33, 13.88) * mm, v(18.03, 12.87) * mm, v(18.6, 12.17) * mm, v(19.14, 12.93) * mm, v(19.17, 13.63) * mm, v(18.85, 14.04) * mm, v(18.76, 14.39) * mm, v(19.62, 14.52) * mm, v(20.54, 14.48) * mm, v(20.95, 14.2) * mm, v(20.57, 13.94) * mm, v(20.1, 13.34) * mm, v(18.8, 11.09) * mm, v(18.12, 10.13) * mm, v(17.1, 10.04) * mm, v(16.12, 11.72) * mm, v(15.52, 12.9) * mm, v(15.04, 12.3) * mm, v(14.44, 11.15) * mm, v(14.57, 10.48) * mm, v(14.6, 10) * mm, v(13.17, 9.91) * mm, v(11.52, 9.85) * mm, v(10.34, 9.85) * mm, v(10.1, 10.26) * mm, v(10.5, 10.61) * mm, v(10.85, 11) * mm, v(10.57, 11.44) * mm, v(9.93, 11.7) * mm, v(8.7, 11.7) * mm, v(8.22, 11.25) * mm, v(8.25, 10.8) * mm, v(8.5, 10.55) * mm, v(8.44, 9.98) * mm, v(7.65, 9.85) * mm]});
            skFitSpline(sketch, "E44", {"points": [v(9.84, 12.3) * mm, v(10.47, 12.3) * mm, v(10.76, 12.36) * mm, v(11.04, 12.58) * mm, v(11.04, 13) * mm, v(11.01, 13.44) * mm, v(10.57, 13.12) * mm, v(10.1, 12.8) * mm, v(9.84, 12.3) * mm]});
            skFitSpline(sketch, "E45", {"points": [v(20.8, 10.1) * mm, v(20.25, 11.21) * mm, v(20.16, 12.67) * mm, v(21.65, 14.23) * mm, v(23.3, 14.7) * mm, v(25.14, 14.45) * mm, v(25.62, 14.1) * mm, v(26, 14.3) * mm, v(26.22, 14.2) * mm, v(26.06, 13.4) * mm, v(25.78, 13.09) * mm, v(25.27, 13.34) * mm, v(24.63, 13.79) * mm, v(23.14, 13.44) * mm, v(22.22, 12.26) * mm, v(22.35, 11.02) * mm, v(22.92, 10.64) * mm, v(23.71, 11.3) * mm, v(23.58, 11.94) * mm, v(23.4, 12.33) * mm, v(24.31, 12.45) * mm, v(25.55, 12.42) * mm, v(25.84, 12.2) * mm, v(25.2, 10.55) * mm, v(24.7, 9.88) * mm, v(24.22, 10.04) * mm, v(23.87, 10.36) * mm, v(22.95, 10.1) * mm, v(21.65, 9.98) * mm, v(20.8, 10.1) * mm]});
            skFitSpline(sketch, "E46", {"points": [v(29.25, 9.9) * mm, v(30.27, 9.9) * mm, v(30.76, 9.9) * mm, v(31.03, 10.23) * mm, v(31.59, 10.93) * mm, v(31.73, 11.18) * mm, v(31.32, 11.28) * mm, v(31.02, 10.9) * mm, v(30.35, 10.63) * mm, v(29.25, 10.42) * mm, v(29.02, 10.51) * mm, v(28.6, 10.51) * mm, v(28.62, 10.7) * mm, v(28.68, 10.82) * mm, v(28.78, 11.01) * mm, v(29.02, 11.68) * mm, v(29.2, 11.7) * mm, v(29.95, 11.64) * mm, v(30.16, 11.56) * mm, v(30.6, 11.46) * mm, v(30.89, 11.97) * mm, v(31.11, 12.43) * mm, v(31.2, 12.65) * mm, v(30.9, 12.76) * mm, v(30.54, 12.5) * mm, v(29.76, 12.41) * mm, v(29.43, 12.45) * mm, v(29.73, 13.2) * mm, v(30.13, 13.8) * mm, v(31.03, 13.92) * mm, v(32.06, 13.33) * mm, v(32.67, 13.13) * mm, v(33.05, 13.87) * mm, v(32.59, 14.4) * mm, v(29.25, 14.53) * mm, v(28.05, 14.47) * mm, v(27.5, 14.49) * mm, v(27.54, 14.06) * mm, v(27.93, 13.6) * mm, v(27.7, 13.4) * mm, v(27.2, 12.32) * mm, v(26.59, 11.13) * mm, v(26.07, 10.51) * mm, v(25.71, 10.43) * mm, v(25.6, 10.01) * mm, v(26.3, 9.9) * mm, v(29.25, 9.9) * mm]});
            skFitSpline(sketch, "E47", {"points": [v(28.78, 10.97) * mm, v(28.77, 10.97) * mm], "startDerivative": vector(-0.02, 0) * mm, "endDerivative": vector(-0.02, 0) * mm});
            skFitSpline(sketch, "E48", {"points": [v(26.9, 14.52) * mm, v(30.72, 14.6) * mm, v(35.69, 14.45) * mm, v(42.88, 14.47) * mm, v(45.37, 14.49) * mm, v(48.2, 14.8) * mm, v(49.5, 14.47) * mm, v(49.87, 14.26) * mm, v(50.17, 14.32) * mm, v(50.47, 14.22) * mm, v(50.3, 13.4) * mm, v(50.1, 13.15) * mm, v(49.68, 13.62) * mm, v(49.1, 14.1) * mm, v(48.36, 14.19) * mm, v(48.17, 13.71) * mm, v(48.98, 12.94) * mm, v(49.68, 12.26) * mm, v(49.5, 10.9) * mm, v(47.41, 9.9) * mm, v(40.84, 9.9) * mm, v(34.33, 8.9) * mm], "startDerivative": vector(53.62, 1.85) * mm, "endDerivative": vector(-67.72, -14.82) * mm});
            skFitSpline(sketch, "E49", {"points": [v(40.84, 9.9) * mm, v(34.46, 9.9) * mm, v(28.05, 9.91) * mm], "startDerivative": vector(-12.77, 0) * mm, "endDerivative": vector(-12.83, 0.01) * mm});
            skFitSpline(sketch, "E50", {"points": [v(32.53, 9.9) * mm, v(32.35, 10.07) * mm, v(32.5, 10.46) * mm, v(32.88, 10.6) * mm, v(33.83, 12.3) * mm, v(34.5, 13.53) * mm, v(34.45, 13.94) * mm, v(34.16, 14.05) * mm, v(34.27, 14.4) * mm, v(34.58, 14.47) * mm, v(37.06, 14.44) * mm, v(37.12, 14.44) * mm, v(37.23, 14.21) * mm, v(36.72, 13.69) * mm, v(35.34, 11.06) * mm, v(35.23, 10.73) * mm, v(35.48, 10.54) * mm, v(36.64, 10.8) * mm, v(37.58, 11.56) * mm, v(37.83, 11.68) * mm, v(37.76, 11.2) * mm, v(37.2, 10.43) * mm, v(36.58, 9.9) * mm], "startDerivative": vector(-8.6, 4.3) * mm, "endDerivative": vector(-12.37, -9.88) * mm});
            skFitSpline(sketch, "E51", {"points": [v(38.72, 9.9) * mm, v(38.27, 10.13) * mm, v(38.38, 10.36) * mm, v(38.95, 10.56) * mm, v(39.64, 11.7) * mm, v(40.3, 12.93) * mm, v(40.62, 13.48) * mm, v(40.55, 13.83) * mm, v(40.2, 14.1) * mm, v(40.26, 14.38) * mm, v(40.56, 14.47) * mm, v(45.1, 14.46) * mm, v(45.68, 14.18) * mm, v(45.54, 13.27) * mm, v(44.83, 13.05) * mm, v(44.3, 13.64) * mm, v(43.75, 13.94) * mm, v(42.81, 13.93) * mm, v(42.39, 13.2) * mm, v(42.15, 12.68) * mm, v(42.19, 12.42) * mm, v(42.98, 12.38) * mm, v(43.4, 12.7) * mm, v(43.67, 12.73) * mm, v(43.65, 12.17) * mm, v(43.3, 11.51) * mm, v(42.75, 11.51) * mm, v(42.46, 11.71) * mm, v(41.73, 11.68) * mm, v(41.47, 11.17) * mm, v(41.17, 10.59) * mm, v(41.71, 10.4) * mm, v(43.01, 10.59) * mm, v(43.73, 11.15) * mm, v(44.2, 11.22) * mm, v(44.01, 10.7) * mm, v(43.61, 10.16) * mm, v(43.27, 9.9) * mm], "startDerivative": vector(-26.23, 7.76) * mm, "endDerivative": vector(-16.01, -11.18) * mm});
            skFitSpline(sketch, "E52", {"points": [v(47.41, 9.9) * mm, v(46.26, 10.25) * mm, v(45.81, 10.44) * mm, v(45.11, 10.4) * mm, v(44.85, 10.53) * mm, v(45.3, 11.7) * mm, v(45.62, 11.86) * mm, v(45.87, 11.36) * mm, v(46.6, 10.75) * mm, v(47.41, 10.8) * mm, v(47.86, 11.22) * mm, v(47.41, 11.6) * mm, v(46.55, 12.2) * mm, v(46.16, 13.36) * mm, v(46.84, 14.4) * mm, v(48.2, 14.8) * mm, v(48.64, 14.76) * mm], "startDerivative": vector(-17.08, 4.17) * mm, "endDerivative": vector(7.73, -1.69) * mm});
            skFitSpline(sketch, "E53", {"points": [v(-23.82, -15.26) * mm, v(-20.95, -19.13) * mm, v(-16.24, -23.7) * mm, v(-10.42, -27.73) * mm, v(-4.86, -30.53) * mm], "startDerivative": vector(11.88, -17.3) * mm, "endDerivative": vector(22.1, -10.12) * mm});
            skFitSpline(sketch, "E54", {"points": [v(-23.81, -15.27) * mm, v(-20.95, -19.13) * mm, v(-16.24, -23.7) * mm, v(-10.42, -27.73) * mm, v(-6.73, -29.13) * mm, v(-4.49, -29.85) * mm, v(-4.13, -29.8) * mm, v(-5.52, -28.06) * mm, v(-8.3, -24.25) * mm, v(-11.2, -19.13) * mm, v(-13.13, -14.76) * mm, v(-13.98, -11.85) * mm, v(-13.62, -11.3) * mm], "startDerivative": vector(26.93, -39.17) * mm, "endDerivative": vector(13.2, 11.63) * mm});
            skFitSpline(sketch, "E55", {"points": [v(-3.45, -29.69) * mm, v(1.04, -30.64) * mm, v(6.73, -30.22) * mm, v(12, -28.98) * mm, v(11.96, -28.3) * mm, v(10.6, -23.7) * mm, v(9.1, -18.7) * mm, v(7.6, -13.95) * mm, v(7.12, -11.43) * mm], "startDerivative": vector(33.2, -9.23) * mm, "endDerivative": vector(-3.32, 23.14) * mm});
            skFitSpline(sketch, "E56", {"points": [v(12.66, -28.72) * mm, v(15.88, -27.26) * mm, v(19.73, -24.7) * mm, v(24.88, -19.64) * mm, v(27.58, -16.18) * mm], "startDerivative": vector(15.08, 6.38) * mm, "endDerivative": vector(9.95, 13.72) * mm});
            skFitSpline(sketch, "E57", {"points": [v(-5.2, 27.05) * mm, v(-3.45, 27.74) * mm, v(-0.54, 27.92) * mm, v(1.94, 27.92) * mm, v(2.83, 28.13) * mm], "startDerivative": vector(6.58, 3.26) * mm, "endDerivative": vector(4.55, 1.46) * mm});
            skFitSpline(sketch, "E58.trimOffspring", {"points": [v(-12.77, 23.5) * mm, v(-10, 25.29) * mm, v(-6.98, 26.53) * mm, v(-5.2, 27.05) * mm], "startDerivative": vector(7.26, 5.17) * mm, "endDerivative": vector(6.07, 1.64) * mm});
            skPoint(sketch, "E59.2.internal.orphan", {"position": v(0, 25.18) * mm});
            skFitSpline(sketch, "E60.trimOffspring", {"points": [v(-17.01, 17) * mm, v(-14.59, 19.07) * mm, v(-12.16, 20.32) * mm, v(-10.51, 21.24) * mm, v(-7.76, 22.66) * mm, v(-5.23, 23.44) * mm, v(-4.01, 23.62) * mm, v(-2.06, 24.2) * mm, v(0.7, 24.58) * mm, v(6.71, 24.84) * mm, v(10.49, 24.34) * mm, v(12.67, 23.62) * mm, v(17.25, 22.06) * mm, v(21.82, 19.76) * mm, v(24.55, 17.74) * mm], "startDerivative": vector(32.04, 30.96) * mm, "endDerivative": vector(33.72, -27.07) * mm});
            skFitSpline(sketch, "E61.trimOffspring", {"points": [v(10.94, 16.14) * mm, v(8.06, 17.85) * mm, v(5.81, 19.45) * mm, v(3.14, 20.95) * mm, v(1.65, 22.12) * mm, v(0.7, 22.98) * mm, v(0.7, 24.58) * mm, v(2.52, 27.25) * mm, v(2.87, 28.52) * mm], "startDerivative": vector(-19.85, 10.94) * mm, "endDerivative": vector(1.16, 12.25) * mm});
            skFitSpline(sketch, "E62", {"points": [v(-4.22, 24.37) * mm, v(-2.76, 24.6) * mm, v(-1.04, 25) * mm, v(0, 25.18) * mm, v(0.71, 25.19) * mm], "startDerivative": vector(5.1, 0.69) * mm, "endDerivative": vector(3.63, -0.07) * mm});
            skFitSpline(sketch, "E63", {"points": [v(30.68, 5.8) * mm, v(30.7, 5.35) * mm, v(30.77, 4.87) * mm, v(30.88, 4.36) * mm, v(30.98, 3.94) * mm, v(31.16, 3.47) * mm], "startDerivative": vector(-0.01, -2.32) * mm, "endDerivative": vector(0.94, -2.37) * mm});
            skPoint(sketch, "E64.2.internal.orphan", {"position": v(-14.44, 22.66) * mm});
            skPoint(sketch, "E64.3.internal.orphan", {"position": v(-13.4, 23.08) * mm});
            skPoint(sketch, "E64.7.internal.orphan", {"position": v(-13.62, 20) * mm});
            skPoint(sketch, "E65.1.internal.orphan", {"position": v(-10.42, 17.37) * mm});
            skPoint(sketch, "E65.2.internal.orphan", {"position": v(-10.42, 18.86) * mm});
            skPoint(sketch, "E65.4.internal.orphan", {"position": v(-11.06, 20.93) * mm});
            skPoint(sketch, "E66.startDerivative.orphan", {"position": v(-10, 17.6) * mm});
            skPoint(sketch, "E67.4.internal.orphan", {"position": v(-4.5, 22.66) * mm});
            skPoint(sketch, "E68.0.internal.orphan", {"position": v(-11.06, 21.9) * mm});
            skPoint(sketch, "E68.1.internal.orphan", {"position": v(-7.76, 23.08) * mm});
            skPoint(sketch, "E68.2.internal.orphan", {"position": v(-5.2, 24) * mm});
            skPoint(sketch, "E68.endDerivative.orphan", {"position": v(-4.5, 24.26) * mm});
            skPoint(sketch, "E69.5.internal.orphan", {"position": v(0, 22.98) * mm});
            skPoint(sketch, "E69.6.internal.orphan", {"position": v(0, 24.52) * mm});
            skPoint(sketch, "E70.1.internal.orphan", {"position": v(-5.2, 25.44) * mm});
            skPoint(sketch, "E71.2.internal.orphan", {"position": v(-1.18, 27.92) * mm});
            skPoint(sketch, "E72.1.internal.orphan", {"position": v(1.53, 26.9) * mm});
            skPoint(sketch, "E73.3.internal.orphan", {"position": v(18.4, 22.98) * mm});
            skFitSpline(sketch, "E74", {"points": [v(-22.48, 14.45) * mm, v(-21.5, 16.08) * mm, v(-19.92, 18.28) * mm, v(-16.26, 22.05) * mm, v(-9.57, 26.16) * mm, v(-3.45, 28.13) * mm, v(4.82, 28.35) * mm, v(12.61, 26.53) * mm, v(17.23, 24.43) * mm, v(21.27, 21.38) * mm, v(25.26, 17.19) * mm, v(26.6, 15.04) * mm, v(27.43, 13.63) * mm, v(27.54, 13.4) * mm, v(27.6, 13.3) * mm], "startDerivative": vector(18.5, 31.15) * mm, "endDerivative": vector(5.36, -7.26) * mm});
            skFitSpline(sketch, "E75", {"points": [v(31.39, -1.6) * mm, v(31.43, -2.13) * mm, v(31.43, -2.82) * mm, v(31.32, -3.93) * mm, v(31.26, -4.33) * mm], "startDerivative": vector(0.21, -2.35) * mm, "endDerivative": vector(-0.28, -1.74) * mm});
            skFitSpline(sketch, "E76", {"points": [v(29.12, 9.9) * mm, v(29.61, 8.9) * mm, v(29.89, 8.26) * mm, v(30.09, 7.63) * mm, v(30.38, 6.7) * mm], "startDerivative": vector(1.84, -3.74) * mm, "endDerivative": vector(1.2, -3.58) * mm});
            skPoint(sketch, "E77.3.internal.orphan", {"position": v(30.23, 7) * mm});
            skSolve(sketch);
        }
        {
            var Q0;
            {var subQ0=sQuery(id+"F0.wireOp",EDGE,"E39");var subQ1=sQuery(id+"F0.wireOp",EDGE,"E38");var subQ2=makeQuery(id+"F0.imprint","INTERSECT",VERTEX,{"disambiguationData":[OD(0.0)],"derivedFrom":[subQ1,subQ0]});Q0=makeQuery(id+"F0.imprint","IMPRINT",FACE,{"disambiguationData":[TD([[makeQuery(id+"F0.imprint","IMPRINT",EDGE,{"disambiguationData":[TD([[subQ2,-1.0]])],"derivedFrom":subQ1}),1.0]])]});}
            var Q1;
            Q1=makeQuery(id+"F0.imprint","IMPRINT",FACE,{"disambiguationData":[TD([[makeQuery(id+"F0.imprint","IMPRINT",EDGE,{"derivedFrom":sQuery(id+"F0.wireOp",EDGE,"E40")}),1.0]])]});
            var Q2;
            Q2=makeQuery(id+"F0.imprint","IMPRINT",FACE,{"disambiguationData":[TD([[makeQuery(id+"F0.imprint","IMPRINT",EDGE,{"derivedFrom":sQuery(id+"F0.wireOp",EDGE,"E42")}),1.0]])]});
            var Q3;
            Q3=makeQuery(id+"F0.imprint","IMPRINT",FACE,{"disambiguationData":[TD([[makeQuery(id+"F0.imprint","IMPRINT",EDGE,{"derivedFrom":sQuery(id+"F0.wireOp",EDGE,"E43")}),-1.0]])]});
            var Q4;
            Q4=makeQuery(id+"F0.imprint","IMPRINT",FACE,{"disambiguationData":[TD([[makeQuery(id+"F0.imprint","IMPRINT",EDGE,{"derivedFrom":sQuery(id+"F0.wireOp",EDGE,"E45")}),-1.0]])]});
            var Q5;
            {var subQ0=sQuery(id+"F0.wireOp",EDGE,"E49");var subQ1=sQuery(id+"F0.wireOp",EDGE,"E46");var subQ12=makeQuery(id+"F0.imprint","INTERSECT",VERTEX,{"disambiguationData":[OD(1.0)],"derivedFrom":[subQ1,subQ0]});Q5=makeQuery(id+"F0.imprint","IMPRINT",FACE,{"disambiguationData":[TD([[makeQuery(id+"F0.imprint","IMPRINT",EDGE,{"disambiguationData":[TD([[subQ12,-1.0]])],"derivedFrom":subQ1}),1.0]])]});}
            var Q6;
            {var subQ0=sQuery(id+"F0.wireOp",EDGE,"E50");var subQ3=sQuery(id+"F0.wireOp",EDGE,"E48");var subQ4=makeQuery(id+"F0.imprint","INTERSECT",VERTEX,{"disambiguationData":[OD(0.0)],"derivedFrom":[subQ3,subQ0]});Q6=makeQuery(id+"F0.imprint","IMPRINT",FACE,{"disambiguationData":[TD([[makeQuery(id+"F0.imprint","IMPRINT",EDGE,{"disambiguationData":[TD([[subQ4,-1.0]])],"derivedFrom":subQ3}),-1.0]])]});}
            var Q7;
            {var subQ0=sQuery(id+"F0.wireOp",EDGE,"E51");var subQ4=sQuery(id+"F0.wireOp",EDGE,"E48");var subQ7=makeQuery(id+"F0.imprint","INTERSECT",VERTEX,{"disambiguationData":[OD(1.0)],"derivedFrom":[subQ4,subQ0]});Q7=makeQuery(id+"F0.imprint","IMPRINT",FACE,{"disambiguationData":[TD([[makeQuery(id+"F0.imprint","IMPRINT",EDGE,{"disambiguationData":[TD([[subQ7,-1.0]])],"derivedFrom":subQ4}),-1.0]])]});}
            var Q8;
            {var subQ0=sQuery(id+"F0.wireOp",EDGE,"E52");var subQ1=sQuery(id+"F0.wireOp",EDGE,"E48");var subQ2=makeQuery(id+"F0.imprint","INTERSECT",VERTEX,{"disambiguationData":[OD(1.0)],"derivedFrom":[subQ1,subQ0]});Q8=makeQuery(id+"F0.imprint","IMPRINT",FACE,{"disambiguationData":[TD([[makeQuery(id+"F0.imprint","IMPRINT",EDGE,{"disambiguationData":[TD([[subQ2,1.0]])],"derivedFrom":subQ1}),-1.0]])]});}
            extrude(context, id + "F1", {"entities" : qUnion([Q0, Q1, Q2, Q3, Q4, Q5, Q6, Q7, Q8]), "depth" : 6.35 * mm});
        }
    });
